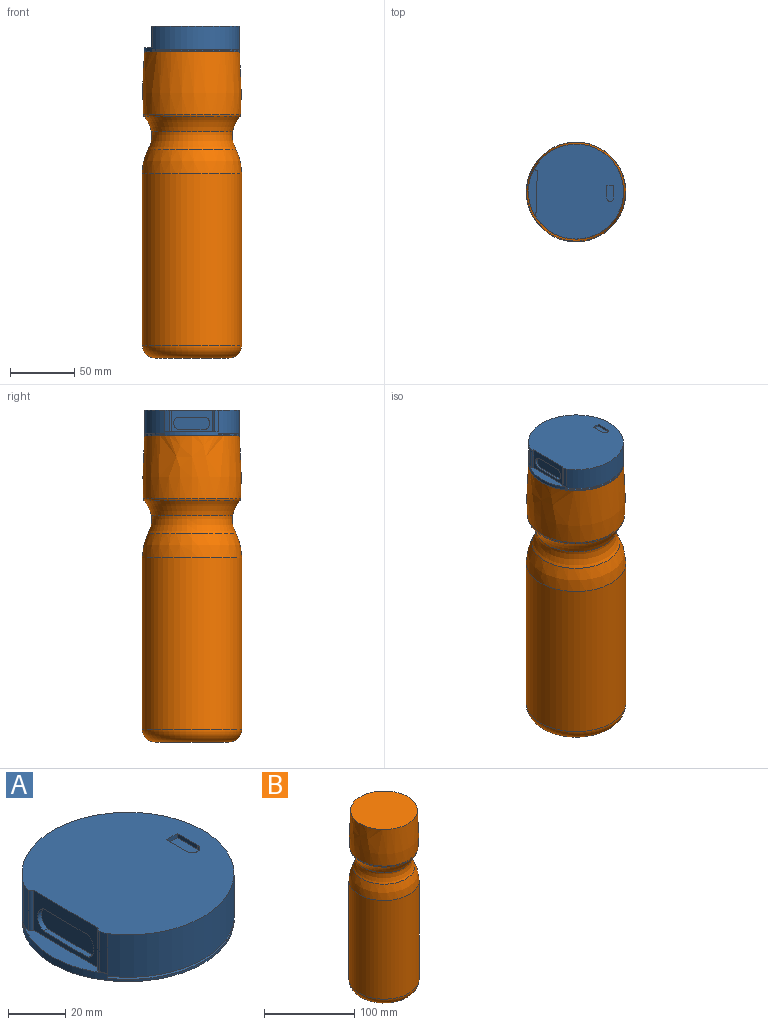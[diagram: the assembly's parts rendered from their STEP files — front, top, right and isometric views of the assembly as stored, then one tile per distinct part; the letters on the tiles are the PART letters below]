
ASSEMBLY  parts=2 mates=1
PART A: 26 faces, bbox 74.2x74x20 mm
  f0: cylinder r=54.04mm len=17mm, axis (0,0,1), area 71.5mm2, adj f1,f10,f11,f24
  f1: cylinder r=1.48mm len=17mm, axis (0,0,1), area 33.2mm2, adj f0,f4,f11,f24
  f2: cylinder r=1.7mm len=17mm, axis (0,0,1), area 36.3mm2, adj f3,f4,f11,f24
  f3: cylinder r=54.04mm len=17mm, axis (0,0,1), area 52.5mm2, adj f2,f10,f11,f24
  f4: plane 32.32x17mm, normal (-1,0.01,0), area 298.9mm2, adj f1,f2,f11,f19,f20,f21,f22,f24
  f5: plane 74.2x74mm, normal (0,0,-1), area 4306.7mm2, adj f6,f25
  f6: cylinder r=37mm len=74mm, axis (0,0,-1), area 181.7mm2, adj f5,f7,f25
  f7: plane 74x67.73mm, normal (0,0,1), area 645.7mm2, adj f6,f8,f17,f18
  f8: cylinder r=33.5mm len=67.01mm, axis (0,0,-1), area 166.4mm2, adj f7,f9,f17,f18
  f9: plane 74x67.73mm, normal (0,0,-1), area 645.7mm2, adj f8,f10,f17,f18
  f10: cylinder r=37mm len=74mm, axis (0,0,-1), area 3406.5mm2, adj f0,f3,f9,f11,f25
  f11: plane 74x68.82mm, normal (0,0,1), area 4059.5mm2, adj f0,f1,f2,f3,f4,f10,f12,f13
  f12: plane 10x1.8mm, normal (1,0,0), area 18mm2, adj f11,f13,f15,f16
  f13: cylinder r=2.66mm len=5.32mm, axis (0,0,1), area 15mm2, adj f11,f12,f14,f16
  f14: plane 10x1.8mm, normal (-1,0,0), area 18mm2, adj f11,f13,f15,f16
  f15: plane 5.32x1.8mm, normal (0,-1,0), area 9.6mm2, adj f11,f12,f14,f16
  f16: plane 12.66x5.32mm, normal (0,0,1), area 64.3mm2, adj f12,f13,f14,f15
  f17: plane 7.09x0.91mm, normal (1,-0.01,0), area 6.5mm2, adj f7,f8,f9,f25
  f18: plane 7.09x0.91mm, normal (1,-0.01,0), area 6.5mm2, adj f7,f8,f9,f25
  f19: plane 22.41x2.23mm, normal (0,0,-1), area 44.8mm2, adj f4,f20,f22,f23
  f20: cylinder r=5.4mm len=9.51mm, axis (-1,0.01,0), area 23.2mm2, adj f4,f19,f21,f23
  f21: plane 22.41x2.23mm, normal (0,0,1), area 44.8mm2, adj f4,f20,f22,f23
  f22: cylinder r=5.51mm len=9.51mm, axis (-1,0.01,0), area 22.9mm2, adj f4,f19,f21,f23
  f23: plane 27.96x9.51mm, normal (-1,0.01,0), area 250.5mm2, adj f19,f20,f21,f22
  f24: plane 41.84x6.9mm, normal (0,0,1), area 183mm2, adj f0,f1,f2,f3,f4,f25
  f25: cylinder r=36.09mm len=41.84mm, axis (0,0,-1), area 133.9mm2, adj f5,f6,f10,f17,f18,f24
PART B: 9 faces, bbox 85.9x85.9x238.8 mm
  f0: torus R=28.8mm, axis (0,0,-1), area 3470.6mm2, adj f1,f8
  f1: cylinder r=38.8mm len=133.75mm, axis (0,0,-1), area 32605.5mm2, adj f0,f2
  f2: revolved ~77.6x77.6mm, area 4610.4mm2, adj f1,f3
  f3: torus R=51.72mm, axis (0,0,-1), area 2863.6mm2, adj f2,f4
  f4: torus R=62.47mm, axis (0,0,-1), area 2770.4mm2, adj f3,f5
  f5: torus R=34.68mm, axis (0,0,-1), area 488.1mm2, adj f4,f6
  f6: revolved ~76.81x76.81mm, area 11701.9mm2, adj f5,f7
  f7: plane 74x74mm, normal (0,0,1), area 4300.8mm2, adj f6
  f8: plane 57.6x57.6mm, normal (0,0,-1), area 2605.4mm2, adj f0
PLACE A t=(-91.11,-38.31,75.6)mm
PLACE B t=(-101.5,-38.31,-153.16)mm
MATE fastened A.f6 <-> B.f0  axis (0,0,-1) through (-91.11,-38.31,55.6)mm
